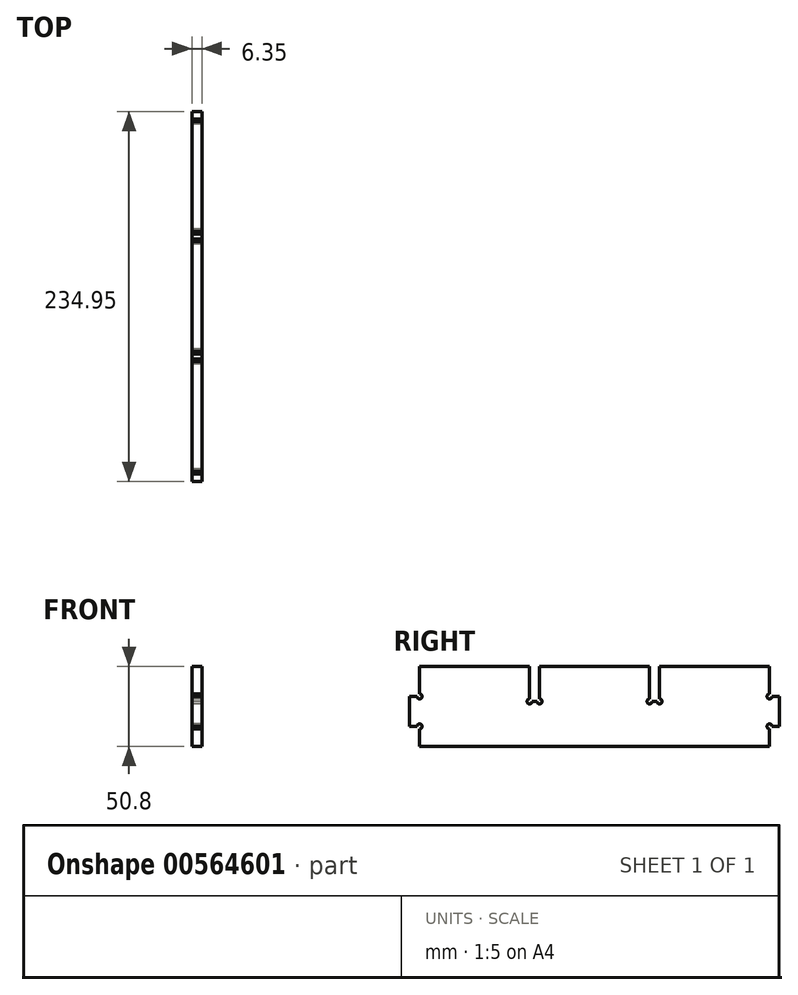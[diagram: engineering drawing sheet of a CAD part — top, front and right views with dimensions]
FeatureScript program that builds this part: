
annotation { "Feature Type Name" : "Feature", "Feature Type Description" : "" }
export const myFeature = defineFeature(function(context is Context, id is Id, definition is map)
    precondition{}
    {
        {
            var Q0;
            Q0=qCreatedBy(makeId("Right.planeOp"),FACE);
            var sketch = newSketch(context, id + "F0", { "sketchPlane" : qUnion([Q0])});
            skLineSegment(sketch, "E0.bottom", {"start": v(-119.29, 22.23) * mm, "end": v(102.96, 22.23) * mm});
            skLineSegment(sketch, "E0.top", {"start": v(-119.29, -28.57) * mm, "end": v(102.96, -28.57) * mm});
            skLineSegment(sketch, "E0.left", {"start": v(-119.29, 22.23) * mm, "end": v(-119.29, -28.57) * mm});
            skLineSegment(sketch, "E0.right", {"start": v(102.96, 22.23) * mm, "end": v(102.96, -28.57) * mm});
            skLineSegment(sketch, "E1.bottom", {"start": v(-49.44, 22.23) * mm, "end": v(-43.09, 22.23) * mm});
            skLineSegment(sketch, "E1.top", {"start": v(-49.44, 0) * mm, "end": v(-43.09, 0) * mm});
            skLineSegment(sketch, "E1.left", {"start": v(-49.44, 22.23) * mm, "end": v(-49.44, 0) * mm});
            skLineSegment(sketch, "E1.right", {"start": v(-43.09, 22.23) * mm, "end": v(-43.09, 0) * mm});
            skLineSegment(sketch, "E2.bottom", {"start": v(26.76, 22.23) * mm, "end": v(33.11, 22.23) * mm});
            skLineSegment(sketch, "E2.top", {"start": v(26.76, 0) * mm, "end": v(33.11, 0) * mm});
            skLineSegment(sketch, "E2.left", {"start": v(26.76, 22.23) * mm, "end": v(26.76, 0) * mm});
            skLineSegment(sketch, "E2.right", {"start": v(33.11, 22.23) * mm, "end": v(33.11, 0) * mm});
            skLineSegment(sketch, "E3.bottom", {"start": v(-119.29, 3.18) * mm, "end": v(-125.64, 3.18) * mm});
            skLineSegment(sketch, "E3.top", {"start": v(-119.29, -15.87) * mm, "end": v(-125.64, -15.87) * mm});
            skLineSegment(sketch, "E3.left", {"start": v(-119.29, 3.18) * mm, "end": v(-119.29, -15.87) * mm});
            skLineSegment(sketch, "E3.right", {"start": v(-125.64, 3.18) * mm, "end": v(-125.64, -15.87) * mm});
            skLineSegment(sketch, "E4.bottom", {"start": v(102.96, 3.18) * mm, "end": v(109.31, 3.18) * mm});
            skLineSegment(sketch, "E4.top", {"start": v(102.96, -15.87) * mm, "end": v(109.31, -15.87) * mm});
            skLineSegment(sketch, "E4.left", {"start": v(102.96, 3.18) * mm, "end": v(102.96, -15.87) * mm});
            skLineSegment(sketch, "E4.right", {"start": v(109.31, 3.18) * mm, "end": v(109.31, -15.87) * mm});
            skPoint(sketch, "E5.visualSharp", {"position": v(-125.64, 3.18) * mm});
            skLineSegment(sketch, "E5.filletArc", {"start": v(-125.64, 3.18) * mm, "end": v(-125.64, 3.18) * mm});
            skPoint(sketch, "E6.visualSharp", {"position": v(-125.64, -15.87) * mm});
            skLineSegment(sketch, "E6.filletArc", {"start": v(-125.64, -15.87) * mm, "end": v(-125.64, -15.87) * mm});
            skPoint(sketch, "E7.visualSharp", {"position": v(-43.09, 0) * mm});
            skLineSegment(sketch, "E7.filletArc", {"start": v(-43.09, 0) * mm, "end": v(-43.09, 0) * mm});
            skPoint(sketch, "E8.visualSharp", {"position": v(-49.44, 0) * mm});
            skLineSegment(sketch, "E8.filletArc", {"start": v(-49.44, 0) * mm, "end": v(-49.44, 0) * mm});
            skPoint(sketch, "E9.visualSharp", {"position": v(33.11, 0) * mm});
            skLineSegment(sketch, "E9.filletArc", {"start": v(33.11, 0) * mm, "end": v(33.11, 0) * mm});
            skPoint(sketch, "E10.visualSharp", {"position": v(26.76, 0) * mm});
            skLineSegment(sketch, "E10.filletArc", {"start": v(26.76, 0) * mm, "end": v(26.76, 0) * mm});
            skPoint(sketch, "E11.visualSharp", {"position": v(109.31, 3.18) * mm});
            skLineSegment(sketch, "E11.filletArc", {"start": v(109.31, 3.18) * mm, "end": v(109.31, 3.18) * mm});
            skPoint(sketch, "E12.visualSharp", {"position": v(109.31, -15.87) * mm});
            skLineSegment(sketch, "E12.filletArc", {"start": v(109.31, -15.87) * mm, "end": v(109.31, -15.87) * mm});
            skCircle(sketch, "E13", {"center": v(-119.29, 3.18) * mm, "radius": 1.59 * mm});
            skCircle(sketch, "E14", {"center": v(-119.29, -15.87) * mm, "radius": 1.59 * mm});
            skCircle(sketch, "E15", {"center": v(-49.44, 0) * mm, "radius": 1.59 * mm});
            skCircle(sketch, "E16", {"center": v(-43.09, 0) * mm, "radius": 1.59 * mm});
            skCircle(sketch, "E17", {"center": v(26.76, 0) * mm, "radius": 1.59 * mm});
            skCircle(sketch, "E18", {"center": v(33.11, 0) * mm, "radius": 1.59 * mm});
            skCircle(sketch, "E19", {"center": v(102.96, 3.18) * mm, "radius": 1.59 * mm});
            skCircle(sketch, "E20", {"center": v(102.96, -15.87) * mm, "radius": 1.59 * mm});
            skSolve(sketch);
        }
        {
            var Q0;
            {var subQ39=sQuery(id+"F0.wireOp",EDGE,"E0.top");Q0=makeQuery(id+"F0.imprint","IMPRINT",FACE,{"disambiguationData":[TD([[makeQuery(id+"F0.imprint","IMPRINT",EDGE,{"derivedFrom":subQ39}),1.0]])]});}
            var Q1;
            {var subQ0=sQuery(id+"F0.wireOp",EDGE,"E3.right");Q1=makeQuery(id+"F0.imprint","IMPRINT",FACE,{"disambiguationData":[TD([[makeQuery(id+"F0.imprint","IMPRINT",EDGE,{"derivedFrom":subQ0}),1.0]])]});}
            var Q2;
            {var subQ0=sQuery(id+"F0.wireOp",EDGE,"E4.right");Q2=makeQuery(id+"F0.imprint","IMPRINT",FACE,{"disambiguationData":[TD([[makeQuery(id+"F0.imprint","IMPRINT",EDGE,{"derivedFrom":subQ0}),-1.0]])]});}
            extrude(context, id + "F1", {"entities" : qUnion([Q0, Q1, Q2]), "depth" : 6.35 * mm, "offsetDistance" : 25.4 * mm});
        }
    });
